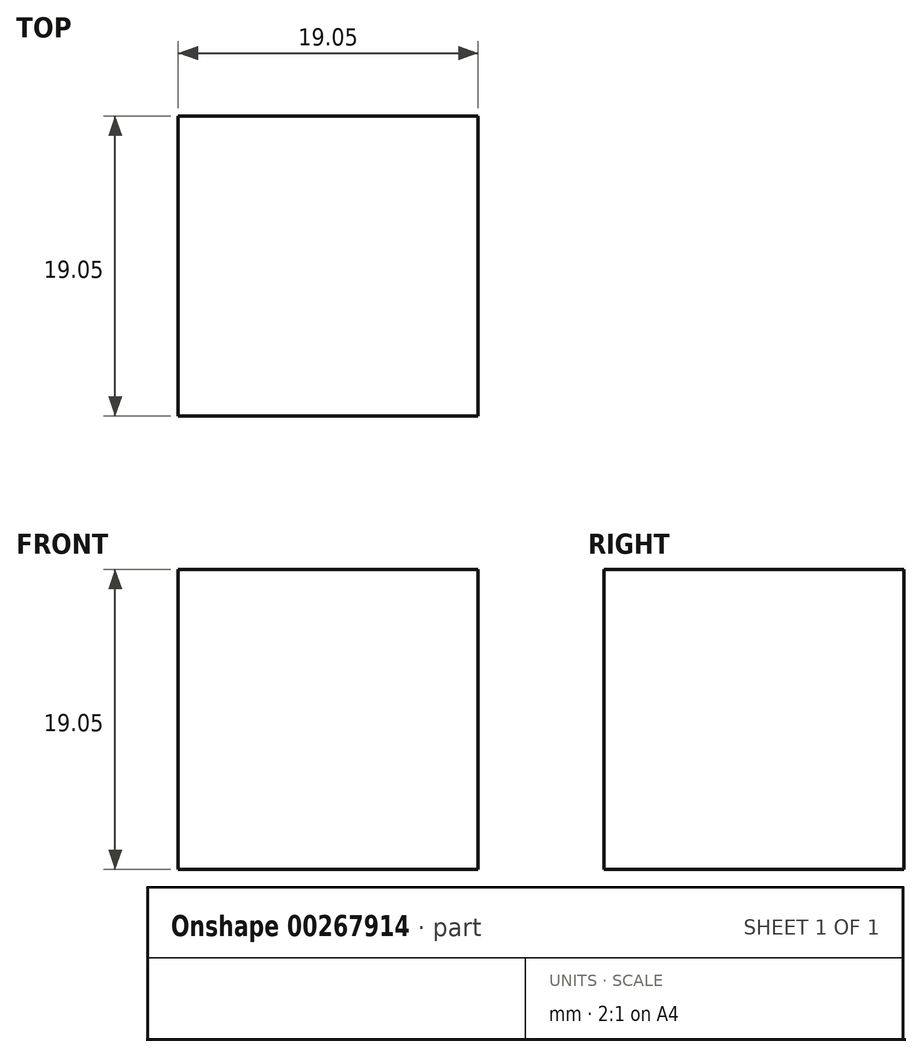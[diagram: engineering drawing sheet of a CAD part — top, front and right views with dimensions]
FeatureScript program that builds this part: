
annotation { "Feature Type Name" : "Feature", "Feature Type Description" : "" }
export const myFeature = defineFeature(function(context is Context, id is Id, definition is map)
    precondition{}
    {
        {
            var Q0;
            Q0=qCreatedBy(makeId("Front.planeOp"),FACE);
            var sketch = newSketch(context, id + "F0", { "sketchPlane" : qUnion([Q0])});
            skLineSegment(sketch, "E0.bottom", {"start": v(0, 0) * mm, "end": v(-19.05, 0) * mm});
            skLineSegment(sketch, "E0.top", {"start": v(0, 19.05) * mm, "end": v(-19.05, 19.05) * mm});
            skLineSegment(sketch, "E0.left", {"start": v(0, 0) * mm, "end": v(0, 19.05) * mm});
            skLineSegment(sketch, "E0.right", {"start": v(-19.05, 0) * mm, "end": v(-19.05, 19.05) * mm});
            skSolve(sketch);
        }
        {
            var Q0;
            Q0 = qSketchRegion(id + "F0", true);
            extrude(context, id + "F1", {"entities" : qUnion([Q0]), "depth" : 19.05 * mm});
        }
    });
